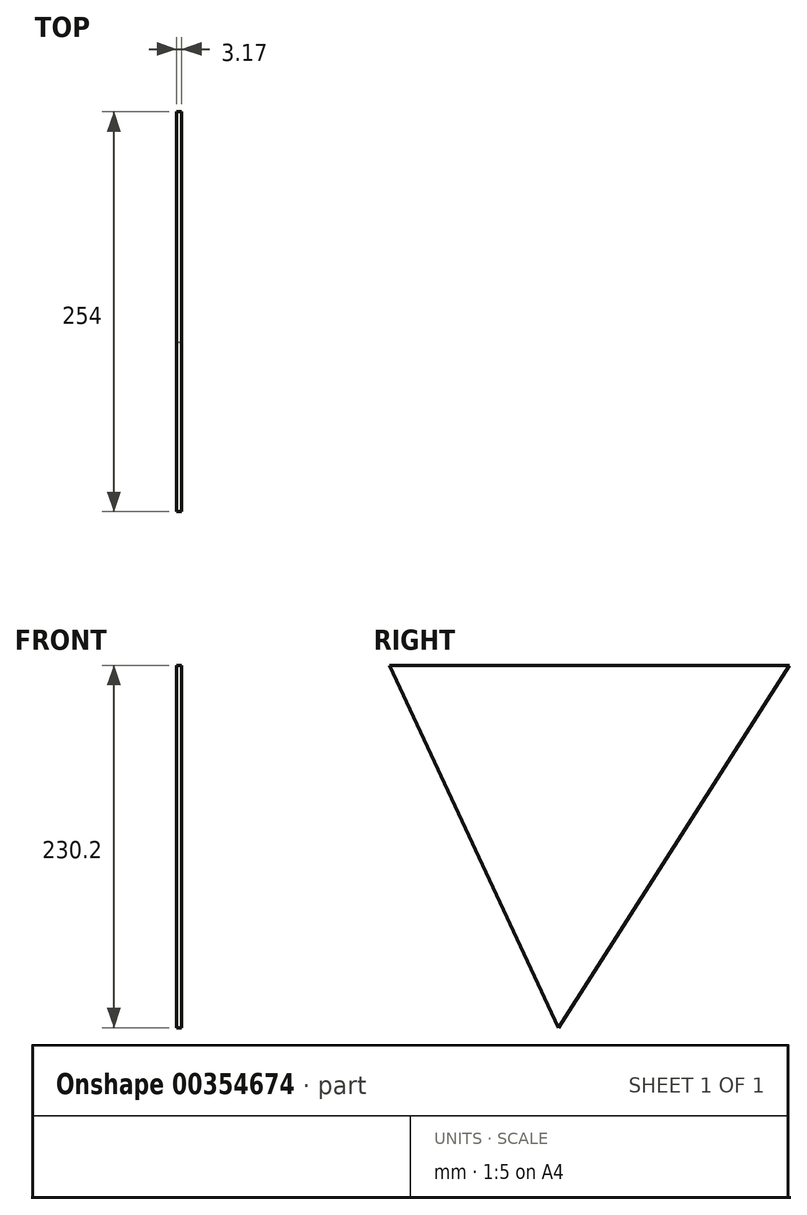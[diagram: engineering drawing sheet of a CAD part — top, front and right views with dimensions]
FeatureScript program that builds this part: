
annotation { "Feature Type Name" : "Feature", "Feature Type Description" : "" }
export const myFeature = defineFeature(function(context is Context, id is Id, definition is map)
    precondition{}
    {
        {
            var Q0;
            Q0=qCreatedBy(makeId("Right.planeOp"),FACE);
            var sketch = newSketch(context, id + "F0", { "sketchPlane" : qUnion([Q0])});
            skLineSegment(sketch, "E0.bottom", {"start": v(127, 127) * mm, "end": v(-127, 127) * mm});
            skPoint(sketch, "E0.middle", {"position": v(0, 0) * mm});
            skPoint(sketch, "E0.top.start.orphan", {"position": v(127, -127) * mm});
            skLineSegment(sketch, "E1", {"start": v(127, 127) * mm, "end": v(127, -127) * mm});
            skLineSegment(sketch, "E2", {"start": v(-127, 127) * mm, "end": v(-19.65, -103.2) * mm});
            skPoint(sketch, "E3.orphan", {"position": v(-127, -127) * mm});
            skLineSegment(sketch, "E4", {"start": v(127, 127) * mm, "end": v(-19.65, -103.2) * mm});
            skSolve(sketch);
        }
        {
            var Q0;
            Q0=qSketchRegion(id+"F0",true);
            extrude(context, id + "F1", {"entities" : qUnion([Q0]), "depth" : 3.17 * mm});
        }
    });
